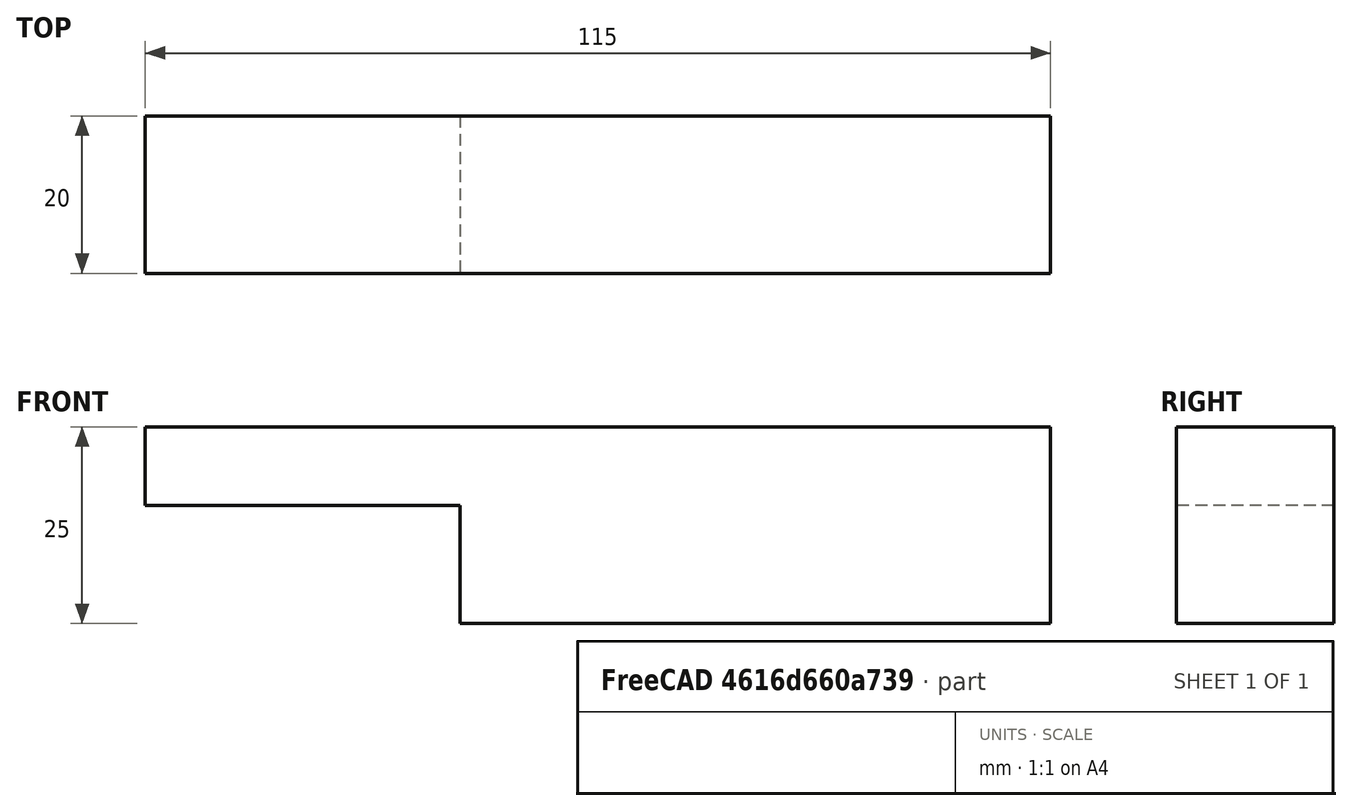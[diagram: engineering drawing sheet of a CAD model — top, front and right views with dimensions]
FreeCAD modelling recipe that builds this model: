
FCSTD DOCUMENT  (FreeCAD 0.20R)
Label: backwardStep
License: All rights reserved
LicenseURL: http://en.wikipedia.org/wiki/All_rights_reserved
objects: Sketcher::SketchObject×1, PartDesign::Pad×1, PartDesign::Body×1
note: 4 computed .brp shape members not serialized (recipe doc carries the construction recipe); baked Part::Feature solids carry a one-line shape summary decoded from their .brp

FEATURE [Sketcher::SketchObject] Sketch
  FullyConstrained = true
  MapMode = 5
  Placement = pos=(0,0,0) rot=(1,0,0;1.5708rad)
  Support = -> [XZ_Plane]
  sketch-geometry (6):
    g0: LineSegment StartX=-40 StartY=10 StartZ=0 EndX=-40 EndY=0 EndZ=0
    g1: LineSegment StartX=-40 StartY=0 StartZ=0 EndX=0 EndY=0 EndZ=0
    g2: LineSegment StartX=0 StartY=0 StartZ=0 EndX=0 EndY=-15 EndZ=0
    g3: LineSegment StartX=0 StartY=-15 StartZ=0 EndX=75 EndY=-15 EndZ=0
    g4: LineSegment StartX=75 StartY=-15 StartZ=0 EndX=75 EndY=10 EndZ=0
    g5: LineSegment StartX=75 StartY=10 StartZ=0 EndX=-40 EndY=10 EndZ=0
  constraints (17):
    c: PointOnObject(g0,g-1)
    c: Vertical(g0)
    c: Coincident(g0,g1)
    c: Coincident(g1,g-1)
    c: Coincident(g1,g2)
    c: Vertical(g2)
    c: Coincident(g2,g3)
    c: Horizontal(g3)
    c: Coincident(g3,g4)
    c: Vertical(g4)
    c: Coincident(g4,g5)
    c: Coincident(g5,g0)
    c: Horizontal(g5)
    c: DistanceX(g0,g4) = 115
    c: DistanceX(g2,g3) = 75
    c: DistanceY(g0,g0) = 10
    c: DistanceY(g3,g4) = 25
FEATURE [PartDesign::Pad] Pad
  Direction = (1,1,1)
  Length = 20
  Length2 = 100
  Placement = pos=(0,0,0) rot=(1,0,0;1.5708rad)
  Profile = -> Sketch
  Type = 0
FEATURE [PartDesign::Body] Body
  Group = -> [Sketch,Pad]
  Origin = -> Origin
  Tip = -> Pad
